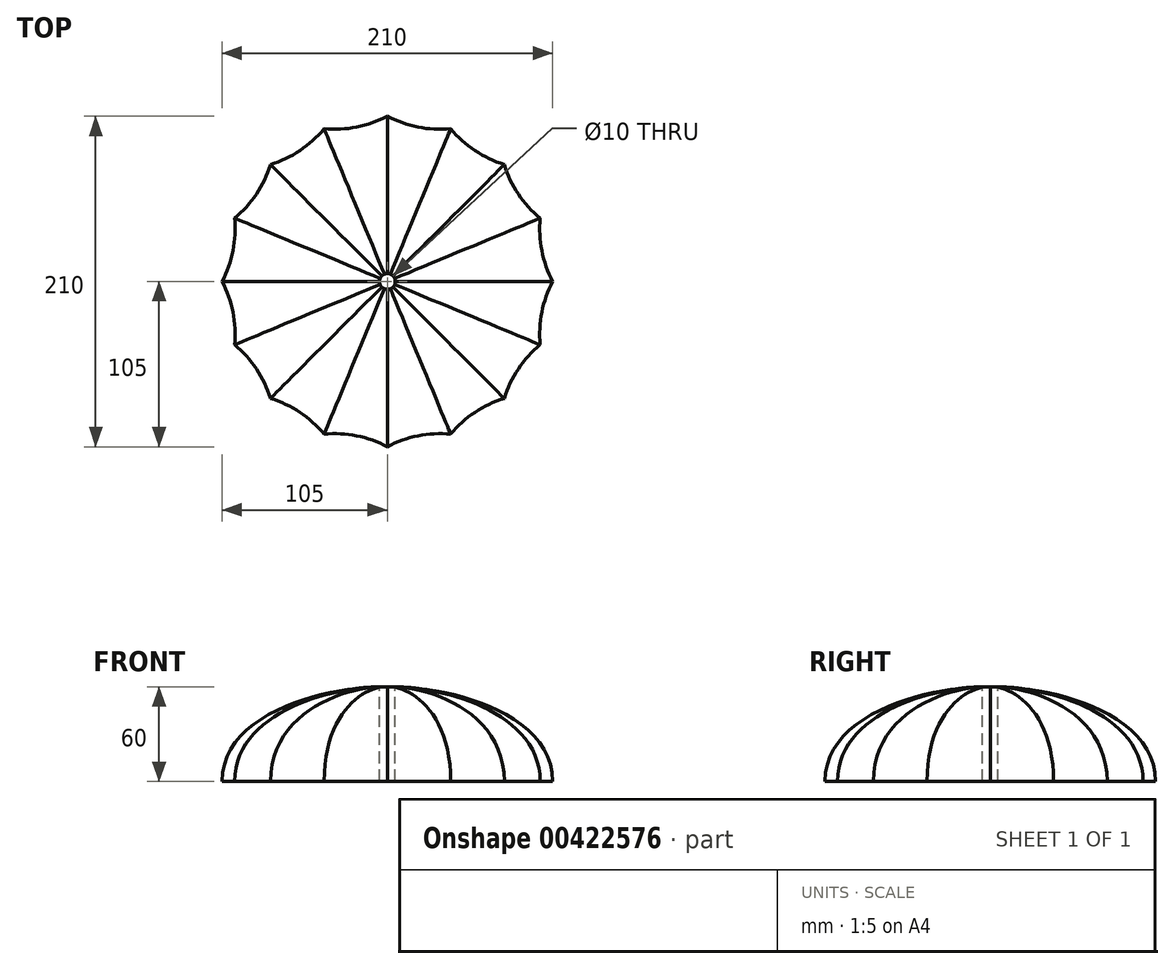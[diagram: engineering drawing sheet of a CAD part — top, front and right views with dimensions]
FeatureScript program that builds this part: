
annotation { "Feature Type Name" : "Feature", "Feature Type Description" : "" }
export const myFeature = defineFeature(function(context is Context, id is Id, definition is map)
    precondition{}
    {
        {
            var Q0;
            Q0=qCreatedBy(makeId("Top.planeOp"),FACE);
            var sketch = newSketch(context, id + "F0", { "sketchPlane" : qUnion([Q0])});
            skCircle(sketch, "E0.cCircle", {"center": v(0, 0) * mm, "radius": 105 * mm, "construction": true});
            skLineSegment(sketch, "E0.0", {"start": v(0, 105) * mm, "end": v(40.18, 97) * mm, "construction": true});
            skLineSegment(sketch, "E0.1", {"start": v(40.18, 97) * mm, "end": v(74.25, 74.25) * mm, "construction": true});
            skLineSegment(sketch, "E0.2", {"start": v(74.25, 74.25) * mm, "end": v(97, 40.18) * mm, "construction": true});
            skLineSegment(sketch, "E0.3", {"start": v(97, 40.18) * mm, "end": v(105, 0) * mm, "construction": true});
            skLineSegment(sketch, "E0.4", {"start": v(105, 0) * mm, "end": v(97, -40.18) * mm, "construction": true});
            skLineSegment(sketch, "E0.5", {"start": v(97, -40.18) * mm, "end": v(74.25, -74.25) * mm, "construction": true});
            skLineSegment(sketch, "E0.6", {"start": v(74.25, -74.25) * mm, "end": v(40.18, -97) * mm, "construction": true});
            skLineSegment(sketch, "E0.7", {"start": v(40.18, -97) * mm, "end": v(0, -105) * mm, "construction": true});
            skLineSegment(sketch, "E0.8", {"start": v(0, -105) * mm, "end": v(-40.18, -97) * mm, "construction": true});
            skLineSegment(sketch, "E0.9", {"start": v(-40.18, -97) * mm, "end": v(-74.25, -74.25) * mm, "construction": true});
            skLineSegment(sketch, "E0.10", {"start": v(-74.25, -74.25) * mm, "end": v(-97, -40.18) * mm, "construction": true});
            skLineSegment(sketch, "E0.11", {"start": v(-97, -40.18) * mm, "end": v(-105, 0) * mm, "construction": true});
            skLineSegment(sketch, "E0.12", {"start": v(-105, 0) * mm, "end": v(-97, 40.18) * mm, "construction": true});
            skLineSegment(sketch, "E0.13", {"start": v(-97, 40.18) * mm, "end": v(-74.25, 74.25) * mm, "construction": true});
            skLineSegment(sketch, "E0.14", {"start": v(-74.25, 74.25) * mm, "end": v(-40.18, 97) * mm, "construction": true});
            skLineSegment(sketch, "E0.15", {"start": v(-40.18, 97) * mm, "end": v(0, 105) * mm, "construction": true});
            skArc(sketch, "E1", {"start": v(0, 105) * mm, "mid": v(19.5, 98.06) * mm, "end": v(40.18, 97) * mm});
            skArc(sketch, "E2.1.17", {"start": v(-40.18, 97) * mm, "mid": v(-19.5, 98.06) * mm, "end": v(0, 105) * mm});
            skArc(sketch, "E2.2.17", {"start": v(-74.25, 74.25) * mm, "mid": v(-55.55, 83.13) * mm, "end": v(-40.18, 97) * mm});
            skArc(sketch, "E2.3.17", {"start": v(-97, 40.18) * mm, "mid": v(-83.13, 55.55) * mm, "end": v(-74.25, 74.25) * mm});
            skArc(sketch, "E2.4.17", {"start": v(-105, 0) * mm, "mid": v(-98.06, 19.5) * mm, "end": v(-97, 40.18) * mm});
            skArc(sketch, "E2.5.17", {"start": v(-97, -40.18) * mm, "mid": v(-98.06, -19.5) * mm, "end": v(-105, 0) * mm});
            skArc(sketch, "E2.6.17", {"start": v(-74.25, -74.25) * mm, "mid": v(-83.13, -55.55) * mm, "end": v(-97, -40.18) * mm});
            skArc(sketch, "E2.7.17", {"start": v(-40.18, -97) * mm, "mid": v(-55.55, -83.13) * mm, "end": v(-74.25, -74.25) * mm});
            skArc(sketch, "E2.8.17", {"start": v(0, -105) * mm, "mid": v(-19.5, -98.06) * mm, "end": v(-40.18, -97) * mm});
            skArc(sketch, "E2.9.17", {"start": v(40.18, -97) * mm, "mid": v(19.5, -98.06) * mm, "end": v(0, -105) * mm});
            skArc(sketch, "E2.10.17", {"start": v(74.25, -74.25) * mm, "mid": v(55.55, -83.13) * mm, "end": v(40.18, -97) * mm});
            skArc(sketch, "E2.11.17", {"start": v(97, -40.18) * mm, "mid": v(83.13, -55.55) * mm, "end": v(74.25, -74.25) * mm});
            skArc(sketch, "E2.12.17", {"start": v(105, 0) * mm, "mid": v(98.06, -19.5) * mm, "end": v(97, -40.18) * mm});
            skArc(sketch, "E2.13.17", {"start": v(97, 40.18) * mm, "mid": v(98.06, 19.5) * mm, "end": v(105, 0) * mm});
            skArc(sketch, "E2.14.17", {"start": v(74.25, 74.25) * mm, "mid": v(83.13, 55.55) * mm, "end": v(97, 40.18) * mm});
            skArc(sketch, "E2.15.17", {"start": v(40.18, 97) * mm, "mid": v(55.55, 83.13) * mm, "end": v(74.25, 74.25) * mm});
            skSolve(sketch);
        }
        {
            var Q0;
            Q0=qCreatedBy(makeId("Top.planeOp"),FACE);
            cPlane(context, id + "F1", {"entities" : qUnion([Q0]), "cplaneType" : CPlaneType.OFFSET, "offset" : 60 * mm, "width" : 150 * mm, "height" : 150 * mm});
        }
        {
            var Q0;
            Q0=qCreatedBy(id+"F1.planeOp",FACE);
            var sketch = newSketch(context, id + "F2", { "sketchPlane" : qUnion([Q0])});
            skCircle(sketch, "E3", {"center": v(0, 0) * mm, "radius": 5 * mm});
            skSolve(sketch);
        }
        {
            var Q0;
            Q0=makeQuery(id+"F0.imprint","IMPRINT",FACE,{"disambiguationData":[TD([[makeQuery(id+"F0.imprint","IMPRINT",EDGE,{"derivedFrom":sQuery(id+"F0.wireOp",EDGE,"E1")}),-1.0]])]});
            var Q1;
            Q1=makeQuery(id+"F2.imprint","IMPRINT",FACE,{"disambiguationData":[TD([[makeQuery(id+"F2.imprint","IMPRINT",EDGE,{"derivedFrom":sQuery(id+"F2.wireOp",EDGE,"E3")}),1.0]])]});
            loft(context, id + "F3", {"startCondition" : LoftEndDerivativeType.NORMAL_TO_PROFILE, "startMagnitude" : 2, "endCondition" : LoftEndDerivativeType.TANGENT_TO_PROFILE, "endMagnitude" : 1, "sheetProfilesArray" : [{ "sheetProfileEntities" : qUnion([Q0]) }, { "sheetProfileEntities" : qUnion([Q1]) }]});
        }
        {
            var Q0;
            Q0=makeQuery(id+"F2.imprint","IMPRINT",FACE,{"disambiguationData":[TD([[makeQuery(id+"F2.imprint","IMPRINT",EDGE,{"derivedFrom":sQuery(id+"F2.wireOp",EDGE,"E3")}),1.0]])]});
            var Q1;
            Q1=makeQuery(id+"F3.opLoft","CAP_FACE",FACE,{"disambiguationData":[OSD([makeQuery(id+"F0.imprint","IMPRINT",FACE,{"disambiguationData":[TD([[makeQuery(id+"F0.imprint","IMPRINT",EDGE,{"derivedFrom":sQuery(id+"F0.wireOp",EDGE,"E1")}),-1.0]])]})])],"isStart":true});
            extrude(context, id + "F4", {"entities" : qUnion([Q0]), "operationType" : NewBodyOperationType.REMOVE, "endBound" : BoundingType.UP_TO_SURFACE, "oppositeDirection" : true, "endBoundEntityFace" : qUnion([Q1]), "depth" : 25 * mm});
        }
    });
